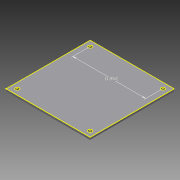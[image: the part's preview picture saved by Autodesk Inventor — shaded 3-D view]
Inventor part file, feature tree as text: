
AUTODESK INVENTOR PART (.ipt)
format: ipt  version: 2015 (Build 190159000, 159)  size: 91,648 bytes
history: native  units: in
note: dims shown in document units (in); Inventor stores cm internally (conversion verified against a paired STEP export)
features: sketch x2, extrude x1, projected_geometry x1
ambient origin geometry x8: Origin, YZ Plane, XZ Plane, XY Plane, X Axis, Y Axis, Z Axis, Center Point
bodies: Solid1 (feature_tree)
feature tree (4):
  extrude  "Extrusion1"  Depth=2.25in
  sketch  "Sketch2"  dims[d2=0.15in d3=0.1in d4=0.15in d5=0.063in d6=0.0in d7=1.95in]
  sketch  "Sketch1"  dims[d0=2.25in d1=2.25in]
  projected_geometry  "Projected Loop1"
